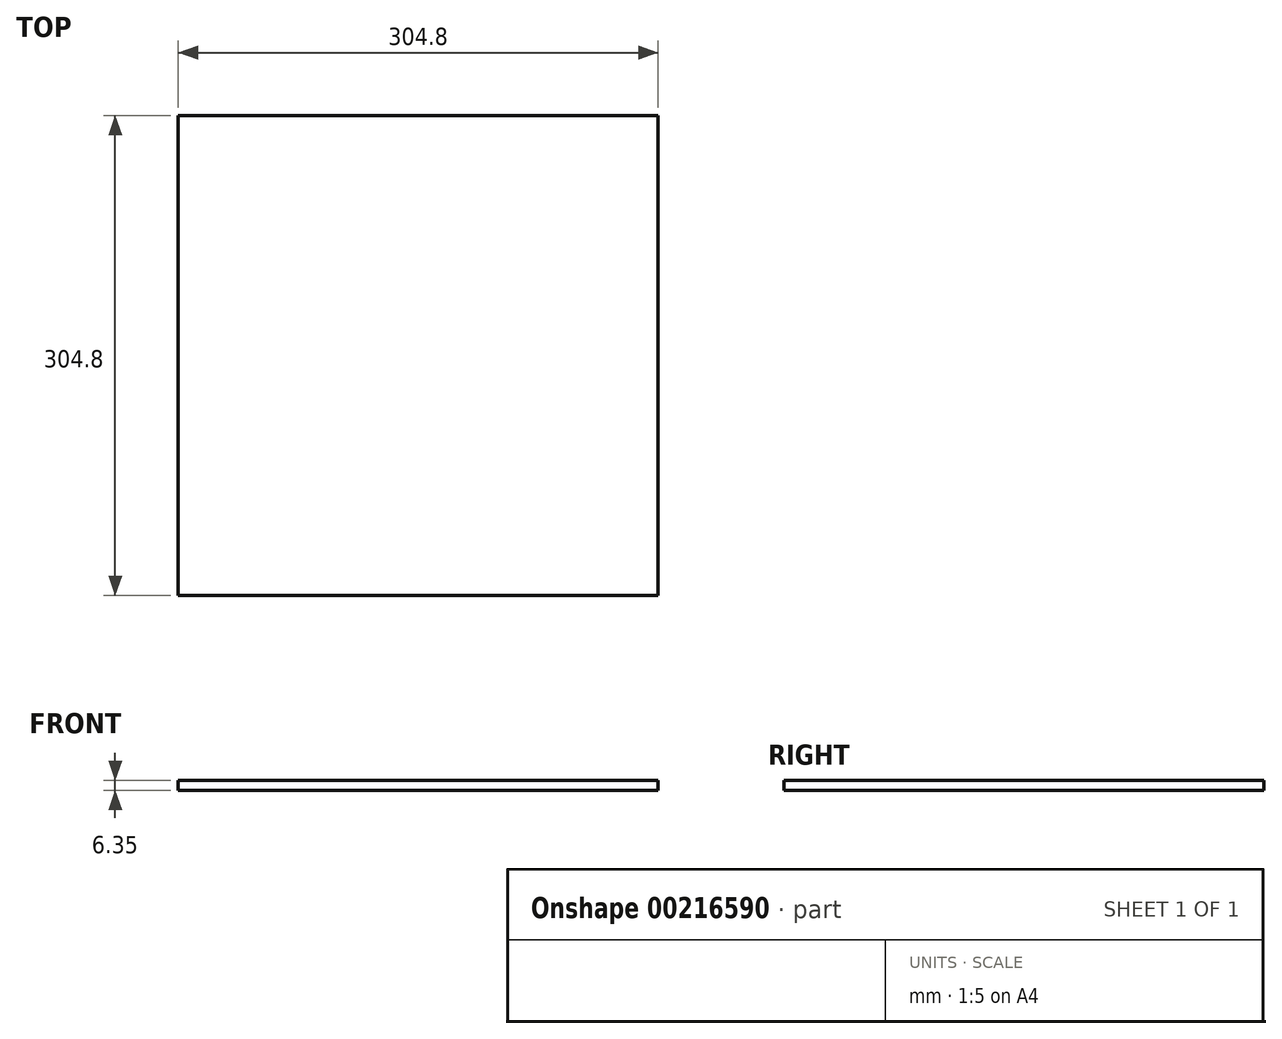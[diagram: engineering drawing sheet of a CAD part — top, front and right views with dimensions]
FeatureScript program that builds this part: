
annotation { "Feature Type Name" : "Feature", "Feature Type Description" : "" }
export const myFeature = defineFeature(function(context is Context, id is Id, definition is map)
    precondition{}
    {
        {
            var Q0;
            Q0=qCreatedBy(makeId("Top.planeOp"),FACE);
            var sketch = newSketch(context, id + "F0", { "sketchPlane" : qUnion([Q0])});
            skLineSegment(sketch, "E0.bottom", {"start": v(-152.4, -152.4) * mm, "end": v(152.4, -152.4) * mm});
            skLineSegment(sketch, "E0.top", {"start": v(-152.4, 152.4) * mm, "end": v(152.4, 152.4) * mm});
            skLineSegment(sketch, "E0.left", {"start": v(-152.4, -152.4) * mm, "end": v(-152.4, 152.4) * mm});
            skLineSegment(sketch, "E0.right", {"start": v(152.4, -152.4) * mm, "end": v(152.4, 152.4) * mm});
            skPoint(sketch, "E0.middle", {"position": v(0, 0) * mm});
            skSolve(sketch);
        }
        {
            var Q0;
            Q0=makeQuery(id+"F0.imprint","IMPRINT",FACE,{"disambiguationData":[TD([[makeQuery(id+"F0.imprint","IMPRINT",EDGE,{"derivedFrom":sQuery(id+"F0.wireOp",EDGE,"E0.bottom")}),1.0]])]});
            extrude(context, id + "F1", {"entities" : qUnion([Q0]), "depth" : 6.35 * mm});
        }
    });
